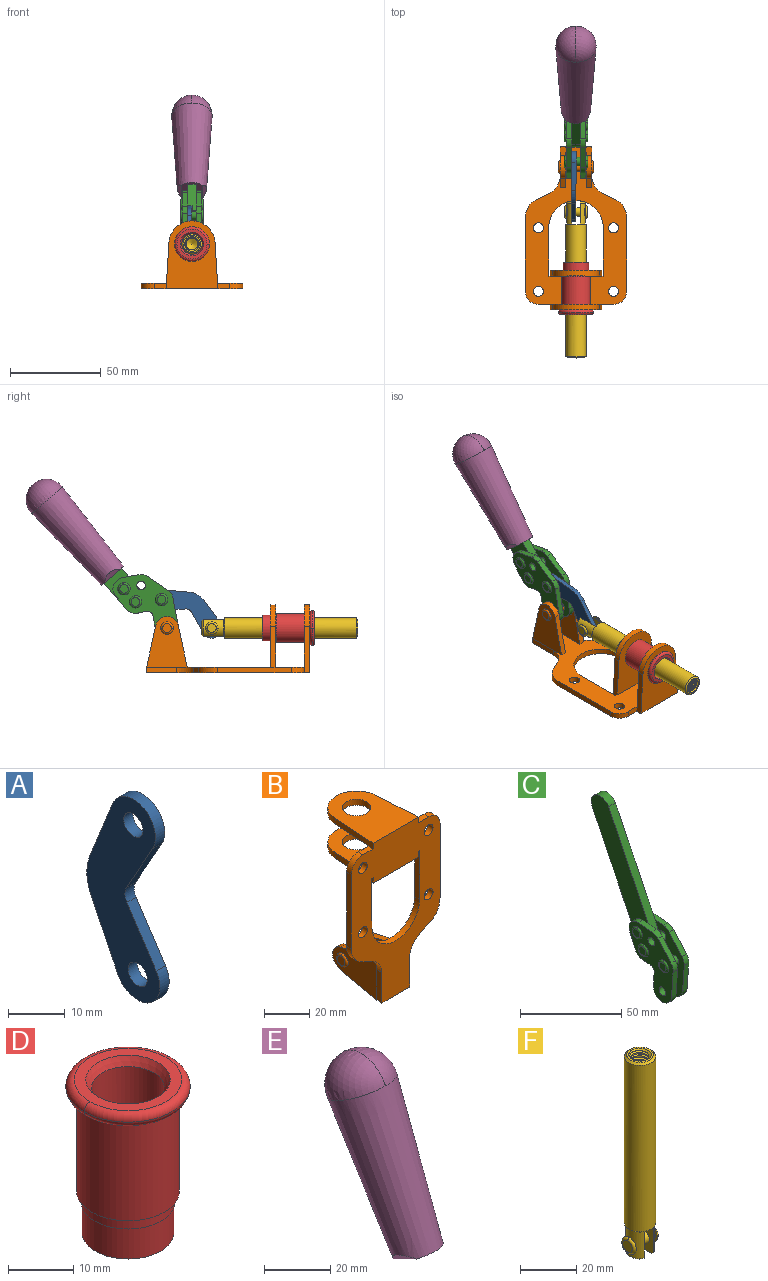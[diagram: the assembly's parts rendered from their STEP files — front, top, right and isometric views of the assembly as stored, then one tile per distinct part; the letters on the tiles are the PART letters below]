
ASSEMBLY  parts=6 mates=6
PART A: 12 faces, bbox 2.3x18.2x42.8 mm
  f0: cylinder r=2.4mm len=4.8mm, axis (1,0,0), area 34.9mm2, adj f4,f11
  f1: cylinder r=10.41mm len=8.47mm, axis (1,0,0), area 20.2mm2, adj f4,f9,f10,f11
  f2: cylinder r=3.05mm len=3.16mm, axis (1,0,0), area 7.7mm2, adj f4,f6,f7,f11
  f3: cylinder r=2.4mm len=4.8mm, axis (1,0,0), area 34.9mm2, adj f4,f11
  f4: plane 42.81x18.23mm, normal (-1,0,0), area 414.1mm2, adj f0,f1,f2,f3,f5,f6,f7,f8
  f5: cylinder r=5.54mm len=10.67mm, axis (1,0,0), area 41.8mm2, adj f4,f6,f10,f11
  f6: plane 11.66x6.53mm, normal (0,-0.87,-0.49), area 30.9mm2, adj f2,f4,f5,f11
  f7: plane 11.17x7.33mm, normal (0,-0.84,0.55), area 30.9mm2, adj f2,f4,f8,f11
  f8: cylinder r=5.54mm len=10.51mm, axis (1,0,0), area 41.8mm2, adj f4,f7,f9,f11
  f9: plane 13.67x6.67mm, normal (0,0.9,-0.44), area 35.1mm2, adj f1,f4,f8,f11
  f10: plane 14.1x5.7mm, normal (0,0.93,0.37), area 35.1mm2, adj f1,f4,f5,f11
  f11: plane 42.81x18.23mm, normal (1,0,0), area 414.1mm2, adj f0,f1,f2,f3,f5,f6,f7,f8
PART B: 55 faces, bbox 55.7x37.4x89.8 mm
  f0: torus R=2.41mm, axis (-1,0,0), area 15mm2, adj f11,f15,f25
  f1: torus R=2.41mm, axis (-1,0,0), area 15mm2, adj f10,f12,f22
  f2: cylinder r=2.78mm len=5.56mm, axis (0,-1,0), area 54.2mm2, adj f30,f54
  f3: cylinder r=14.99mm len=29.97mm, axis (0,-1,0), area 145.9mm2, adj f30,f49,f53,f54
  f4: cylinder r=2.78mm len=5.56mm, axis (0,-1,0), area 54.2mm2, adj f30,f54
  f5: cylinder r=2.78mm len=5.56mm, axis (0,-1,0), area 54.2mm2, adj f30,f54
  f6: cylinder r=2.78mm len=5.56mm, axis (0,-1,0), area 54.2mm2, adj f30,f54
  f7: cylinder r=6.35mm len=12.7mm, axis (0,0,1), area 123.6mm2, adj f27,f51
  f8: cylinder r=6.35mm len=12.7mm, axis (0,0,-1), area 124.7mm2, adj f21,f35
  f9: cylinder r=2.41mm len=11.18mm, axis (-1,0,0), area 169.4mm2, adj f16,f19
  f10: plane 4.83x4.83mm, normal (1,0,0), area 18.3mm2, adj f1,f12
  f11: plane 4.83x4.83mm, normal (-1,0,0), area 18.3mm2, adj f0,f15
  f12: torus R=2.41mm, axis (-1,0,0), area 15mm2, adj f1,f10,f22
  f13: cylinder r=6.35mm len=12.41mm, axis (1,0,0), area 53.4mm2, adj f18,f19,f22,f23
  f14: cylinder r=6.35mm len=12.41mm, axis (-1,0,0), area 53.4mm2, adj f16,f17,f24,f25
  f15: torus R=2.41mm, axis (-1,0,0), area 15mm2, adj f0,f11,f25
  f16: plane 27.86x22.35mm, normal (1,0,0), area 425.4mm2, adj f9,f14,f17,f24,f30
  f17: plane 22.86x4.97mm, normal (0,0.21,0.98), area 72.5mm2, adj f14,f16,f25,f30
  f18: plane 22.86x4.97mm, normal (0,0.21,0.98), area 72.5mm2, adj f13,f19,f22,f30
  f19: plane 27.86x22.35mm, normal (-1,0,0), area 425.4mm2, adj f9,f13,f18,f23,f30
  f20: cylinder r=12.7mm len=25.35mm, axis (0,0,-1), area 119.8mm2, adj f21,f34,f35,f36
  f21: plane 34.21x28.07mm, normal (0,0,-1), area 702.4mm2, adj f8,f20,f30,f34,f36
  f22: plane 27.96x22.45mm, normal (1,0,0), area 407.2mm2, adj f1,f12,f13,f18,f23,f30,f42,f43
  f23: plane 22.86x4.97mm, normal (0,0.21,-0.98), area 72.5mm2, adj f13,f19,f22,f44
  f24: plane 22.86x4.97mm, normal (0,0.21,-0.98), area 72.5mm2, adj f14,f16,f25,f44
  f25: plane 27.86x22.35mm, normal (-1,0,0), area 407.1mm2, adj f0,f14,f15,f17,f24,f30,f45,f46
  f26: plane 3.1x0.95mm, normal (0,0,-1), area 2.7mm2, adj f30,f49,f50,f54
  f27: plane 34.21x28.07mm, normal (0,0,1), area 702.4mm2, adj f7,f28,f30,f50,f52
  f28: cylinder r=12.7mm len=25.35mm, axis (0,0,1), area 118.8mm2, adj f27,f50,f51,f52
  f29: plane 3.1x0.95mm, normal (0,0,-1), area 2.7mm2, adj f30,f52,f53,f54
  f30: plane 86.54x55.63mm, normal (0,1,0), area 2362.9mm2, adj f2,f3,f4,f5,f6,f16,f17,f18
  f31: plane 40.56x3.1mm, normal (-1,0,0), area 125.7mm2, adj f30,f32,f48,f54
  f32: cylinder r=7.11mm len=7.11mm, axis (0,-1,0), area 34.6mm2, adj f30,f31,f33,f54
  f33: plane 6.67x3.1mm, normal (0,0,1), area 20.4mm2, adj f30,f32,f34,f54
  f34: plane 25.39x3.13mm, normal (-1,0.06,0), area 79.5mm2, adj f20,f21,f33,f35,f54
  f35: plane 37.31x28.45mm, normal (0,0,1), area 789.9mm2, adj f8,f20,f34,f36,f54
  f36: plane 25.39x3.13mm, normal (1,0.06,0), area 79.5mm2, adj f20,f21,f35,f37,f54
  f37: plane 6.67x3.1mm, normal (0,0,1), area 20.4mm2, adj f30,f36,f38,f54
  f38: cylinder r=7.11mm len=7.11mm, axis (0,-1,0), area 34.6mm2, adj f30,f37,f39,f54
  f39: plane 40.56x3.1mm, normal (1,0,0), area 125.7mm2, adj f30,f38,f40,f54
  f40: cylinder r=11.18mm len=10.16mm, axis (0,-1,0), area 39.5mm2, adj f30,f39,f41,f54
  f41: plane 6.09x3.1mm, normal (0.42,0,-0.91), area 20.8mm2, adj f30,f40,f42,f54
  f42: cylinder r=11.18mm len=9.41mm, axis (0,-1,0), area 37.2mm2, adj f22,f30,f41,f43,f54
  f43: plane 16.5x3.1mm, normal (1,0,0), area 51.1mm2, adj f22,f42,f44,f54
  f44: plane 17.37x3.1mm, normal (0,0,-1), area 53.8mm2, adj f23,f24,f30,f43,f45,f54
  f45: plane 16.5x3.1mm, normal (-1,0,0), area 51.1mm2, adj f25,f44,f46,f54
  f46: cylinder r=11.18mm len=9.41mm, axis (0,-1,0), area 37.2mm2, adj f25,f30,f45,f47,f54
  f47: plane 6.09x3.1mm, normal (-0.42,0,-0.91), area 20.8mm2, adj f30,f46,f48,f54
  f48: cylinder r=11.18mm len=10.16mm, axis (0,-1,0), area 39.5mm2, adj f30,f31,f47,f54
  f49: plane 26.54x3.1mm, normal (-1,0,0), area 82.3mm2, adj f3,f26,f30,f54
  f50: plane 25.39x3.1mm, normal (1,0.06,0), area 78.8mm2, adj f26,f27,f28,f51,f54
  f51: plane 37.31x28.45mm, normal (0,0,-1), area 789.9mm2, adj f7,f28,f50,f52,f54
  f52: plane 25.39x3.1mm, normal (-1,0.06,0), area 78.8mm2, adj f27,f28,f29,f51,f54
  f53: plane 26.54x3.1mm, normal (1,0,0), area 82.3mm2, adj f3,f29,f30,f54
  f54: plane 89.66x55.63mm, normal (0,-1,0), area 2678.5mm2, adj f2,f3,f4,f5,f6,f26,f29,f31
PART C: 59 faces, bbox 12.9x60.2x99.6 mm
  f0: torus R=2.39mm, axis (-1,0,0), area 14.9mm2, adj f20,f43,f51
  f1: torus R=2.39mm, axis (-1,0,0), area 14.9mm2, adj f19,f42,f51
  f2: torus R=2.39mm, axis (-1,0,0), area 14.9mm2, adj f18,f35,f51
  f3: torus R=2.39mm, axis (-1,0,0), area 14.9mm2, adj f14,f17,f23
  f4: torus R=2.39mm, axis (-1,0,0), area 14.9mm2, adj f13,f16,f23
  f5: torus R=2.39mm, axis (-1,0,0), area 14.9mm2, adj f12,f15,f23
  f6: cylinder r=2.39mm len=4.78mm, axis (1,0,0), area 46.5mm2, adj f48,f50,f51
  f7: cylinder r=2.39mm len=4.78mm, axis (1,0,0), area 46.5mm2, adj f50,f51
  f8: cylinder r=6.35mm len=12.68mm, axis (1,0,0), area 61.8mm2, adj f38,f39,f50,f51
  f9: cylinder r=2.39mm len=4.78mm, axis (-1,0,0), area 70.5mm2, adj f46,f50
  f10: cylinder r=2.39mm len=4.78mm, axis (-1,0,0), area 46.5mm2, adj f23,f45,f46
  f11: cylinder r=2.39mm len=4.78mm, axis (-1,0,0), area 46.5mm2, adj f23,f46
  f12: plane 4.78x4.78mm, normal (1,0,0), area 17.9mm2, adj f5,f15
  f13: plane 4.78x4.78mm, normal (1,0,0), area 17.9mm2, adj f4,f16
  f14: plane 4.78x4.78mm, normal (1,0,0), area 17.9mm2, adj f3,f17
  f15: torus R=2.39mm, axis (-1,0,0), area 14.9mm2, adj f5,f12,f23
  f16: torus R=2.39mm, axis (-1,0,0), area 14.9mm2, adj f4,f13,f23
  f17: torus R=2.39mm, axis (-1,0,0), area 14.9mm2, adj f3,f14,f23
  f18: plane 4.78x4.78mm, normal (-1,0,0), area 17.9mm2, adj f2,f35
  f19: plane 4.78x4.78mm, normal (-1,0,0), area 17.9mm2, adj f1,f42
  f20: plane 4.78x4.78mm, normal (-1,0,0), area 17.9mm2, adj f0,f43
  f21: plane 2.26x0.2mm, normal (1,0,0), area 0.2mm2, adj f31,f44
  f22: plane 2.26x0.2mm, normal (-1,0,0), area 0.2mm2, adj f41,f44
  f23: plane 39.37x30.77mm, normal (1,0,0), area 565.5mm2, adj f3,f4,f5,f10,f11,f15,f16,f17
  f24: cylinder r=6.1mm len=4.15mm, axis (-1,0,0), area 14.7mm2, adj f23,f25,f32,f46
  f25: plane 10.25x9.01mm, normal (0,-0.75,0.66), area 42.3mm2, adj f23,f24,f26,f46
  f26: cylinder r=6.35mm len=4.64mm, axis (-1,0,0), area 15.6mm2, adj f23,f25,f27,f46
  f27: plane 15.84x3.1mm, normal (0,-1,-0.07), area 49.2mm2, adj f23,f26,f28,f46
  f28: cylinder r=6.35mm len=12.68mm, axis (-1,0,0), area 61.8mm2, adj f23,f27,f29,f46
  f29: plane 8.11x3.1mm, normal (0,1,0.07), area 25.2mm2, adj f23,f28,f30,f46
  f30: cylinder r=3.05mm len=3.25mm, axis (-1,0,0), area 14.8mm2, adj f23,f29,f31,f46
  f31: plane 5.99x3.1mm, normal (0,0.07,-1), area 18.6mm2, adj f21,f23,f30,f44,f46
  f32: plane 9.5x3.1mm, normal (0,-0.07,1), area 29.5mm2, adj f23,f24,f33,f46,f47
  f33: cylinder r=6.1mm len=8.63mm, axis (-1,0,0), area 39.1mm2, adj f23,f32,f34,f47
  f34: plane 8.65x3.96mm, normal (0,0.91,-0.42), area 29.5mm2, adj f23,f33,f44,f47
  f35: torus R=2.39mm, axis (-1,0,0), area 14.9mm2, adj f2,f18,f51
  f36: plane 10.25x9.01mm, normal (0,-0.75,0.66), area 42.3mm2, adj f37,f49,f50,f51
  f37: cylinder r=6.35mm len=4.64mm, axis (1,0,0), area 15.6mm2, adj f36,f38,f50,f51
  f38: plane 15.84x3.1mm, normal (0,-1,-0.07), area 49.2mm2, adj f8,f37,f50,f51
  f39: plane 8.11x3.1mm, normal (0,1,0.07), area 25.2mm2, adj f8,f40,f50,f51
  f40: cylinder r=3.05mm len=3.25mm, axis (1,0,0), area 14.8mm2, adj f39,f41,f50,f51
  f41: plane 5.99x3.1mm, normal (0,0.07,-1), area 18.6mm2, adj f22,f40,f44,f50,f51
  f42: torus R=2.39mm, axis (-1,0,0), area 14.9mm2, adj f1,f19,f51
  f43: torus R=2.39mm, axis (-1,0,0), area 14.9mm2, adj f0,f20,f51
  f44: cylinder r=6.35mm len=12.12mm, axis (-1,0,0), area 128.9mm2, adj f21,f22,f23,f31,f34,f41,f46,f47
  f45: plane 2.65x1.35mm, normal (1,0,0), area 1mm2, adj f10,f55
  f46: plane 39.08x20.42mm, normal (-1,0,0), area 412.5mm2, adj f9,f10,f11,f24,f25,f26,f27,f28
  f47: plane 77.62x39.82mm, normal (1,0,0), area 850mm2, adj f32,f33,f34,f44,f53,f54,f55
  f48: plane 2.65x1.35mm, normal (-1,0,0), area 1mm2, adj f6,f55
  f49: cylinder r=6.1mm len=4.15mm, axis (1,0,0), area 14.7mm2, adj f36,f50,f51,f56
  f50: plane 39.08x20.42mm, normal (1,0,0), area 412.5mm2, adj f6,f7,f8,f9,f36,f37,f38,f39
  f51: plane 39.37x30.77mm, normal (-1,0,0), area 565.5mm2, adj f0,f1,f2,f6,f7,f8,f35,f36
  f52: plane 8.65x3.96mm, normal (0,0.91,-0.42), area 29.5mm2, adj f44,f51,f57,f58
  f53: plane 68.49x33.4mm, normal (0,0.9,-0.44), area 358.1mm2, adj f44,f47,f54,f58
  f54: cylinder r=6.35mm len=12.06mm, axis (1,0,0), area 93.7mm2, adj f47,f53,f55,f58
  f55: plane 68.49x33.4mm, normal (0,-0.9,0.44), area 358.1mm2, adj f44,f45,f46,f47,f48,f50,f54,f58
  f56: plane 9.5x3.1mm, normal (0,-0.07,1), area 29.5mm2, adj f49,f50,f51,f57,f58
  f57: cylinder r=6.1mm len=8.63mm, axis (1,0,0), area 39.1mm2, adj f51,f52,f56,f58
  f58: plane 77.62x39.82mm, normal (-1,0,0), area 850mm2, adj f44,f52,f53,f54,f55,f56,f57
PART D: 15 faces, bbox 20.6x20.6x28.7 mm
  f0: torus R=8.26mm, axis (0,0,1), area 56.8mm2, adj f1,f10,f12
  f1: torus R=8.26mm, axis (0,0,1), area 56.8mm2, adj f0,f6,f13
  f2: cylinder r=5.59mm len=25.91mm, axis (0,0,1), area 909.6mm2, adj f3,f4
  f3: cone r=6.86mm half-angle=45deg, axis (0,0,-1), area 70.2mm2, adj f2,f14
  f4: cone r=6.47mm half-angle=30deg, axis (0,0,1), area 66.7mm2, adj f2,f13
  f5: cylinder r=7.04mm len=14.07mm, axis (0,0,1), area 252.6mm2, adj f11,f14
  f6: torus R=8.26mm, axis (0,0,1), area 56.8mm2, adj f1,f12,f13
  f7: cylinder r=7.16mm len=14.33mm, axis (0,0,1), area 91.5mm2, adj f9,f11
  f8: cylinder r=7.86mm len=18.42mm, axis (0,0,1), area 909.6mm2, adj f9,f10
  f9: plane 15.72x15.72mm, normal (0,0,-1), area 33mm2, adj f7,f8
  f10: plane 16.51x16.51mm, normal (0,0,-1), area 19.9mm2, adj f0,f8,f12
  f11: plane 14.33x14.33mm, normal (0,0,-1), area 5.7mm2, adj f5,f7
  f12: torus R=8.26mm, axis (0,0,1), area 56.8mm2, adj f0,f6,f10
  f13: plane 16.51x16.51mm, normal (0,0,1), area 82.7mm2, adj f1,f4,f6
  f14: plane 14.07x14.07mm, normal (0,0,-1), area 7.8mm2, adj f3,f5
PART E: 11 faces, bbox 22.3x42.6x64.5 mm
  f0: sphere r=11.13mm, area 411.4mm2, adj f1,f8
  f1: cone r=11.11mm half-angle=3.3deg, axis (0,0.44,0.9), area 3251.8mm2, adj f0,f7,f8,f9,f10
  f2: cylinder r=6.16mm len=11.7mm, axis (1,0,0), area 89.5mm2, adj f3,f4,f5,f6
  f3: plane 60.23x36.75mm, normal (-1,0,0), area 763.6mm2, adj f2,f4,f6,f10
  f4: plane 51.37x25.05mm, normal (0,0.9,-0.44), area 264.2mm2, adj f2,f3,f5,f10
  f5: plane 60.23x36.75mm, normal (1,0,0), area 763.6mm2, adj f2,f4,f6,f10
  f6: plane 51.37x25.05mm, normal (0,-0.9,0.44), area 264.2mm2, adj f2,f3,f5,f10
  f7: plane 9.95x5.95mm, normal (0.71,-0.31,-0.64), area 25.8mm2, adj f1,f10
  f8: sphere r=11.13mm, area 411.4mm2, adj f0,f1
  f9: plane 9.95x5.95mm, normal (-0.71,-0.31,-0.64), area 25.8mm2, adj f1,f10
  f10: plane 14.27x11.38mm, normal (0,-0.44,-0.9), area 106.7mm2, adj f1,f3,f4,f5,f6,f7,f9
PART F: 48 faces, bbox 12.6x11.1x86.1 mm
  f0: torus R=2.41mm, axis (-1,0,0), area 15mm2, adj f30,f32,f34
  f1: torus R=2.41mm, axis (-1,0,0), area 15mm2, adj f29,f31,f33
  f2: cylinder r=5.54mm len=72.39mm, axis (0,0,1), area 2518.5mm2, adj f3,f4,f42,f43
  f3: cone r=5.54mm half-angle=45deg, axis (0,0,1), area 7.6mm2, adj f2,f5,f41
  f4: cone r=5.54mm half-angle=45deg, axis (0,0,-1), area 34.9mm2, adj f2,f39
  f5: cylinder r=5.08mm len=11.48mm, axis (0,0,1), area 108.3mm2, adj f3,f7,f8,f41
  f6: cylinder r=2.41mm len=4.83mm, axis (-1,0,0), area 71.2mm2, adj f40,f41
  f7: cylinder r=2.41mm len=4.83mm, axis (-1,0,0), area 7.6mm2, adj f5,f34
  f8: cone r=5.08mm half-angle=45deg, axis (0,0,1), area 10.6mm2, adj f5,f37,f41
  f9: cone r=3.98mm half-angle=45deg, axis (0,0,1), area 17.6mm2, adj f27,f39,f45,f46,f47
  f10: cylinder r=2.41mm len=4.83mm, axis (-1,0,0), area 7.6mm2, adj f33,f38
  f11: cylinder r=3.2mm len=6.4mm, axis (0,0,1), area 78.4mm2, adj f12,f28,f44,f45,f47
  f12: cylinder r=3.2mm len=6.4mm, axis (0,0,1), area 10.5mm2, adj f11,f13,f45,f47
  f13: cylinder r=3.2mm len=6.4mm, axis (0,0,1), area 10.5mm2, adj f12,f14,f45,f47
  f14: cylinder r=3.2mm len=6.4mm, axis (0,0,1), area 10.5mm2, adj f13,f15,f45,f47
  f15: cylinder r=3.2mm len=6.4mm, axis (0,0,1), area 10.5mm2, adj f14,f16,f45,f47
  f16: cylinder r=3.2mm len=6.4mm, axis (0,0,1), area 10.5mm2, adj f15,f17,f45,f47
  f17: cylinder r=3.2mm len=6.4mm, axis (0,0,1), area 10.5mm2, adj f16,f18,f45,f47
  f18: cylinder r=3.2mm len=6.4mm, axis (0,0,1), area 10.5mm2, adj f17,f19,f45,f47
  f19: cylinder r=3.2mm len=6.4mm, axis (0,0,1), area 10.5mm2, adj f18,f20,f45,f47
  f20: cylinder r=3.2mm len=6.4mm, axis (0,0,1), area 10.5mm2, adj f19,f21,f45,f47
  f21: cylinder r=3.2mm len=6.4mm, axis (0,0,1), area 10.5mm2, adj f20,f22,f45,f47
  f22: cylinder r=3.2mm len=6.4mm, axis (0,0,1), area 10.5mm2, adj f21,f23,f45,f47
  f23: cylinder r=3.2mm len=6.4mm, axis (0,0,1), area 10.5mm2, adj f22,f24,f45,f47
  f24: cylinder r=3.2mm len=6.4mm, axis (0,0,1), area 10.5mm2, adj f23,f25,f45,f47
  f25: cylinder r=3.2mm len=6.4mm, axis (0,0,1), area 10.5mm2, adj f24,f26,f45,f47
  f26: cylinder r=3.2mm len=6.4mm, axis (0,0,1), area 10.5mm2, adj f25,f27,f45,f47
  f27: cylinder r=3.2mm len=6.4mm, axis (0,0,1), area 7.4mm2, adj f9,f26,f45,f47
  f28: cone r=3.2mm half-angle=60deg, axis (0,0,1), area 37.2mm2, adj f11
  f29: plane 4.83x4.83mm, normal (-1,0,0), area 18.3mm2, adj f1,f31
  f30: plane 4.83x4.83mm, normal (1,0,0), area 18.3mm2, adj f0,f32
  f31: torus R=2.41mm, axis (-1,0,0), area 15mm2, adj f1,f29,f33
  f32: torus R=2.41mm, axis (-1,0,0), area 15mm2, adj f0,f30,f34
  f33: plane 6.83x6.83mm, normal (1,0,0), area 18.3mm2, adj f1,f10,f31
  f34: plane 6.83x6.83mm, normal (-1,0,0), area 18.3mm2, adj f0,f7,f32
  f35: cone r=5.08mm half-angle=45deg, axis (0,0,1), area 10.6mm2, adj f36,f38,f40
  f36: plane 7.25x1.97mm, normal (0,0,-1), area 10mm2, adj f35,f40
  f37: plane 7.25x1.97mm, normal (0,0,-1), area 10mm2, adj f8,f41
  f38: cylinder r=5.08mm len=11.48mm, axis (0,0,1), area 108.3mm2, adj f10,f35,f40,f42
  f39: plane 9.55x9.55mm, normal (0,0,1), area 22mm2, adj f4,f9
  f40: plane 12.76x10.09mm, normal (1,0,0), area 95.7mm2, adj f6,f35,f36,f38,f42,f43
  f41: plane 12.76x10.09mm, normal (-1,0,0), area 95.7mm2, adj f3,f5,f6,f8,f37,f43
  f42: cone r=5.54mm half-angle=45deg, axis (0,0,1), area 7.6mm2, adj f2,f38,f40
  f43: plane 11.07x4.7mm, normal (0,0,-1), area 50.4mm2, adj f2,f40,f41
  f44: plane 0.89x0.62mm, normal (-1,0,0), area 0.3mm2, adj f11,f45,f46,f47
  f45: bspline ~24.8x7.63mm, area 266.6mm2, adj f9,f11,f12,f13,f14,f15,f16,f17
  f46: bspline ~24.87x7.63mm, area 73.6mm2, adj f9,f44,f45,f47
  f47: bspline ~24.98x7.63mm, area 272.5mm2, adj f9,f11,f12,f13,f14,f15,f16,f17
PLACE A rot(axis=(0,-0.52,-0.85),180deg) t=(-1.16,42.14,11.22)mm
PLACE B rot(axis=(1,0,0),90deg) t=(0,9.43,0)mm fixed
PLACE C rot(axis=(-1,0,0),15deg) t=(0,26.05,61.98)mm
PLACE D rot(axis=(1,0,0),90deg) t=(0,9.43,0)mm
PLACE E rot(axis=(-1,0,0),15deg) t=(-0.04,26.05,61.98)mm
PLACE F rot(axis=(1,0,0),90deg) t=(0,32.36,0)mm
MATE revolute C.f4 <-> A.f0  axis (-1,0,0) through (0,44.55,40.2)mm
MATE fastened E.f2 <-> C.f54  axis (1,0,0) through (-2.35,108.85,96.5)mm
MATE slider F.f2 <-> B.f7  axis (0,-1,0) through (0,-26.42,24.61)mm
MATE fastened D.f2 <-> B.f7  axis (0,-1,0) through (0,-36.96,24.61)mm
MATE revolute A.f3 <-> F.f6  axis (-1,0,0) through (0,16.89,24.61)mm
MATE revolute C.f7 <-> B.f0  axis (1,0,0) through (0,41.52,24.61)mm
